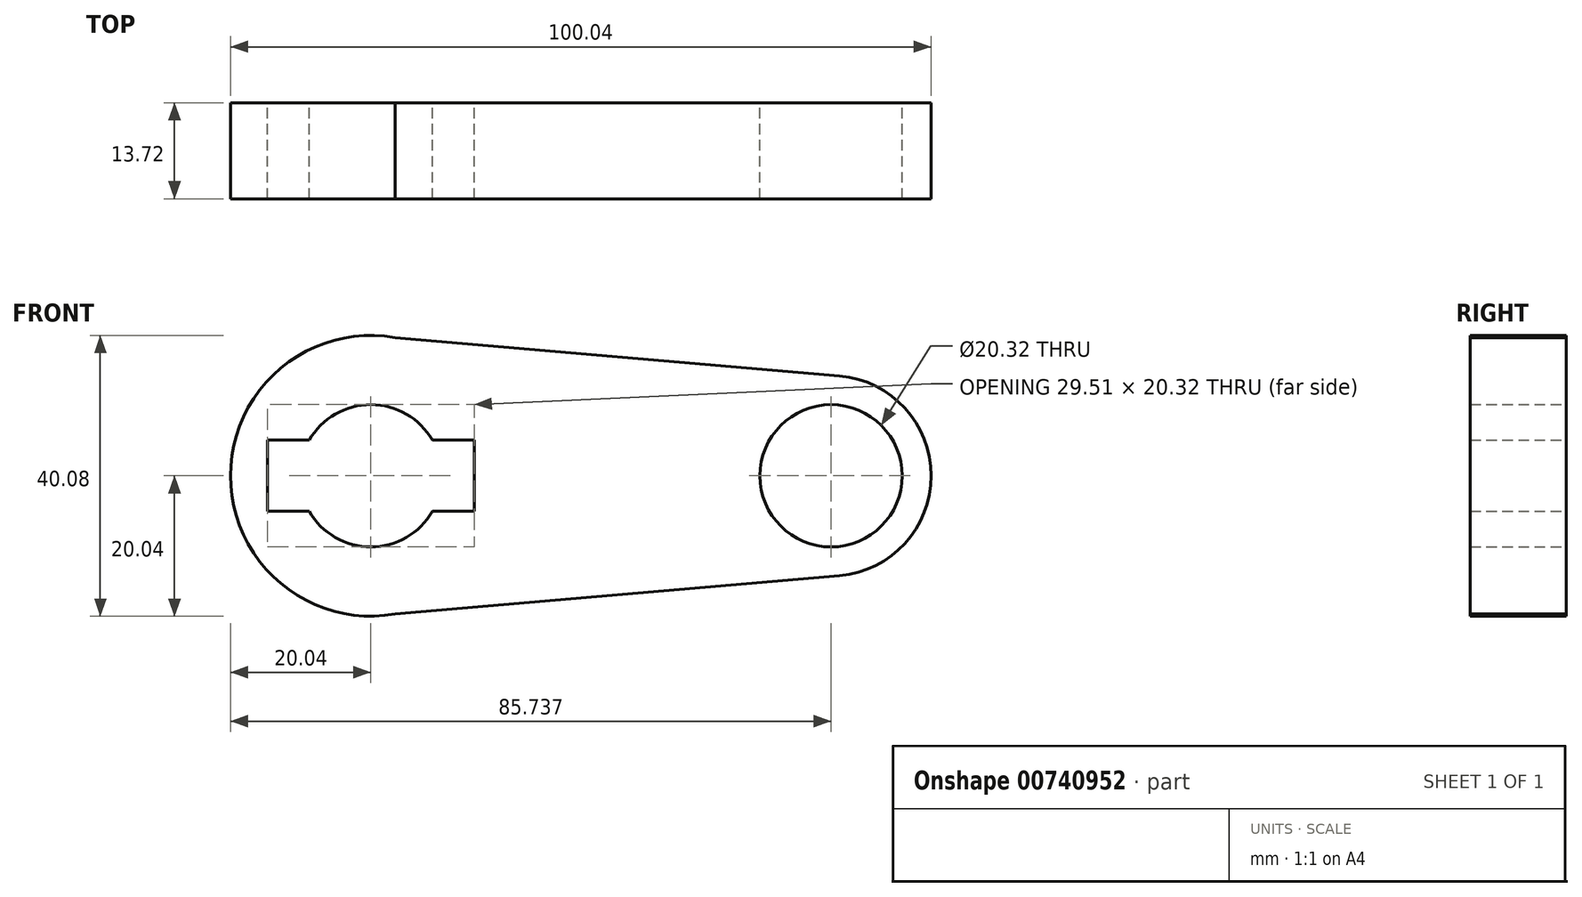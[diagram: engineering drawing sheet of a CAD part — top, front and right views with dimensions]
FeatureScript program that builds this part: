
annotation { "Feature Type Name" : "Feature", "Feature Type Description" : "" }
export const myFeature = defineFeature(function(context is Context, id is Id, definition is map)
    precondition{}
    {
        {
            var Q0;
            Q0=qCreatedBy(makeId("Front.planeOp"),FACE);
            var sketch = newSketch(context, id + "F0", { "sketchPlane" : qUnion([Q0])});
            skCircle(sketch, "E0", {"center": v(0, 0) * mm, "radius": 20.04 * mm});
            skCircle(sketch, "E1", {"center": v(65.7, 0) * mm, "radius": 14.3 * mm});
            skLineSegment(sketch, "E2", {"start": v(0, 20.04) * mm, "end": v(66.93, 14.25) * mm});
            skLineSegment(sketch, "E3", {"start": v(0, -20.04) * mm, "end": v(72.18, -13.8) * mm});
            skCircle(sketch, "E4", {"center": v(0, 0) * mm, "radius": 10.16 * mm});
            skCircle(sketch, "E5", {"center": v(65.7, 0) * mm, "radius": 10.16 * mm});
            skLineSegment(sketch, "E6.bottom", {"start": v(-14.75, 5.08) * mm, "end": v(14.75, 5.08) * mm});
            skLineSegment(sketch, "E6.top", {"start": v(-14.75, -5.08) * mm, "end": v(14.75, -5.08) * mm});
            skLineSegment(sketch, "E6.left", {"start": v(-14.75, 5.08) * mm, "end": v(-14.75, -5.08) * mm});
            skLineSegment(sketch, "E6.right", {"start": v(14.75, 5.08) * mm, "end": v(14.75, -5.08) * mm});
            skSolve(sketch);
        }
        {
            var Q0;
            Q0 = qSketchRegion(id + "F0", true);
            extrude(context, id + "F1", {"entities" : qUnion([Q0]), "depth" : 13.72 * mm, "offsetDistance" : 25.4 * mm});
        }
    });
